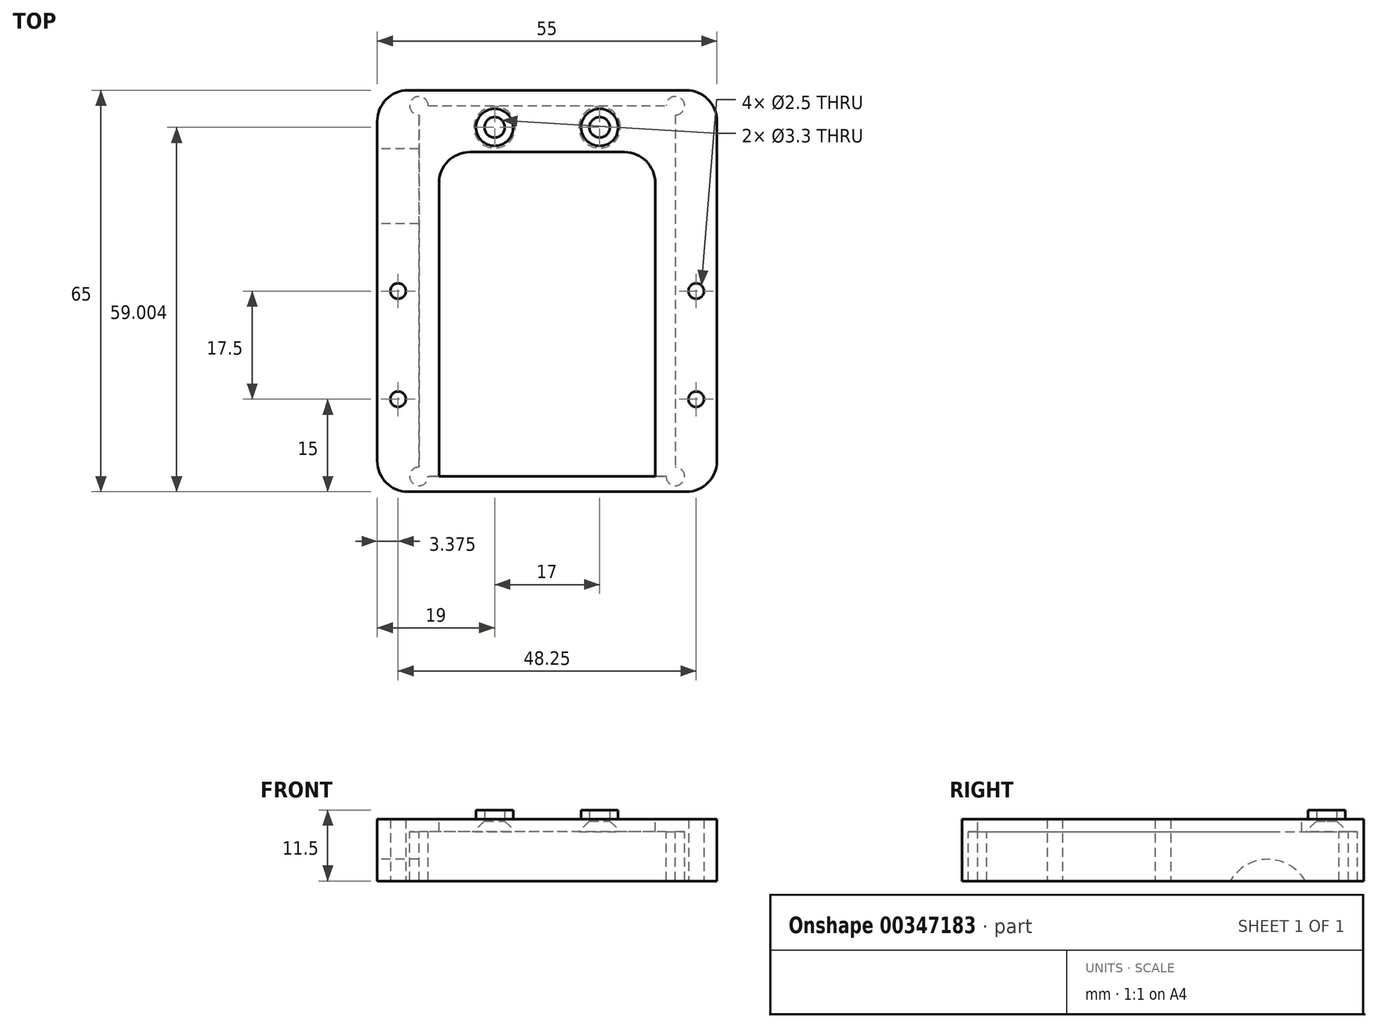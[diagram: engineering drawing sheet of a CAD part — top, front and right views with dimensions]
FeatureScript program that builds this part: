
annotation { "Feature Type Name" : "Feature", "Feature Type Description" : "" }
export const myFeature = defineFeature(function(context is Context, id is Id, definition is map)
    precondition{}
    {
        {
            var Q0;
            Q0=qCreatedBy(makeId("Front.planeOp"),FACE);
            var sketch = newSketch(context, id + "F0", { "sketchPlane" : qUnion([Q0])});
            skLineSegment(sketch, "E0.bottom", {"start": v(27.5, -5) * mm, "end": v(-27.5, -5) * mm});
            skLineSegment(sketch, "E0.top", {"start": v(27.5, 5) * mm, "end": v(-27.5, 5) * mm});
            skLineSegment(sketch, "E0.left", {"start": v(27.5, -5) * mm, "end": v(27.5, 5) * mm});
            skLineSegment(sketch, "E0.right", {"start": v(-27.5, -5) * mm, "end": v(-27.5, 5) * mm});
            skPoint(sketch, "E0.middle", {"position": v(0, 0) * mm});
            skSolve(sketch);
        }
        {
            var Q0;
            Q0 = qSketchRegion(id + "F0", true);
            extrude(context, id + "F1", {"entities" : qUnion([Q0]), "endBound" : BoundingType.SYMMETRIC, "depth" : 65 * mm});
        }
        {
            var Q0;
            Q0=qCreatedBy(makeId("Top.planeOp"),FACE);
            var sketch = newSketch(context, id + "F2", { "sketchPlane" : qUnion([Q0])});
            skPoint(sketch, "E1.middle", {"position": v(0, 0) * mm});
            skPoint(sketch, "E2.visualSharp", {"position": v(17.5, 22.5) * mm});
            skPoint(sketch, "E3.visualSharp", {"position": v(-17.5, 22.5) * mm});
            skLineSegment(sketch, "E4", {"start": v(-17.5, 17.5) * mm, "end": v(-17.5, -30) * mm});
            skLineSegment(sketch, "E5", {"start": v(17.5, 17.5) * mm, "end": v(17.5, -30) * mm});
            skLineSegment(sketch, "E6", {"start": v(17.5, -30) * mm, "end": v(-17.5, -30) * mm});
            skLineSegment(sketch, "E7", {"start": v(-12.5, 22.5) * mm, "end": v(12.5, 22.5) * mm});
            skArc(sketch, "E8.filletArc", {"start": v(17.5, 17.5) * mm, "mid": v(16.04, 21.04) * mm, "end": v(12.5, 22.5) * mm});
            skArc(sketch, "E9.filletArc", {"start": v(-12.5, 22.5) * mm, "mid": v(-16.04, 21.04) * mm, "end": v(-17.5, 17.5) * mm});
            skSolve(sketch);
        }
        {
            var Q0;
            Q0=makeQuery(id+"F1.opExtrude","CAP_EDGE",EDGE,{"disambiguationData":[OSD([sQuery(id+"F0.wireOp",EDGE,"E0.left")])],"isStart":false});
            var Q1;
            Q1=makeQuery(id+"F1.opExtrude","CAP_EDGE",EDGE,{"disambiguationData":[OSD([sQuery(id+"F0.wireOp",EDGE,"E0.right")])],"isStart":false});
            var Q2;
            Q2=makeQuery(id+"F1.opExtrude","CAP_EDGE",EDGE,{"disambiguationData":[OSD([sQuery(id+"F0.wireOp",EDGE,"E0.right")])],"isStart":true});
            var Q3;
            Q3=makeQuery(id+"F1.opExtrude","CAP_EDGE",EDGE,{"disambiguationData":[OSD([sQuery(id+"F0.wireOp",EDGE,"E0.left")])],"isStart":true});
            fillet(context, id + "F3", {"entities" : qUnion([Q0, Q1, Q2, Q3]), "radius" : 5 * mm, "tangentPropagation" : true, "allowEdgeOverflow" : false});
        }
        {
            var Q0;
            Q0 = qSketchRegion(id + "F2", true);
            var Q1;
            Q1=makeQuery(id+"F1.opExtrude","SWEPT_FACE",FACE,{"disambiguationData":[OSD([sQuery(id+"F0.wireOp",EDGE,"E0.top")])]});
            extrude(context, id + "F4", {"entities" : qUnion([Q0]), "operationType" : NewBodyOperationType.REMOVE, "endBound" : BoundingType.SYMMETRIC, "oppositeDirection" : true, "endBoundEntityFace" : qUnion([Q1]), "depth" : 25 * mm});
        }
        {
            var Q0;
            Q0=qCreatedBy(makeId("Top.planeOp"),FACE);
            var sketch = newSketch(context, id + "F5", { "sketchPlane" : qUnion([Q0])});
            skLineSegment(sketch, "E10.bottom", {"start": v(20.75, -30) * mm, "end": v(-20.75, -30) * mm});
            skLineSegment(sketch, "E10.top", {"start": v(20.75, 30) * mm, "end": v(-20.75, 30) * mm});
            skLineSegment(sketch, "E10.left", {"start": v(20.75, -30) * mm, "end": v(20.75, 30) * mm});
            skLineSegment(sketch, "E10.right", {"start": v(-20.75, -30) * mm, "end": v(-20.75, 30) * mm});
            skPoint(sketch, "E10.middle", {"position": v(0, 0) * mm});
            skCircle(sketch, "E11", {"center": v(-20.75, 30) * mm, "radius": 1.5 * mm});
            skCircle(sketch, "E12", {"center": v(20.75, 30) * mm, "radius": 1.5 * mm});
            skCircle(sketch, "E13", {"center": v(-20.75, -30) * mm, "radius": 1.5 * mm});
            skCircle(sketch, "E14", {"center": v(20.75, -30) * mm, "radius": 1.5 * mm});
            skSolve(sketch);
        }
        {
            var Q0;
            Q0 = qSketchRegion(id + "F5", true);
            extrude(context, id + "F6", {"entities" : qUnion([Q0]), "operationType" : NewBodyOperationType.REMOVE, "oppositeDirection" : true, "depth" : 30 * mm});
        }
        {
            var Q0;
            Q0 = qSketchRegion(id + "F5", true);
            extrude(context, id + "F7", {"entities" : qUnion([Q0]), "operationType" : NewBodyOperationType.REMOVE, "depth" : 3 * mm});
        }
        {
            var Q0;
            Q0=makeQuery(id+"F7.boolean.opBoolean","COPY",FACE,{"derivedFrom":makeQuery(id+"F7.opExtrude","CAP_FACE",FACE,{"disambiguationData":[OSD([sQuery(id+"F5.wireOp",EDGE,"E10.bottom"),sQuery(id+"F5.wireOp",EDGE,"E10.top"),sQuery(id+"F5.wireOp",EDGE,"E10.left"),sQuery(id+"F5.wireOp",EDGE,"E10.right"),sQuery(id+"F5.wireOp",EDGE,"E11"),sQuery(id+"F5.wireOp",EDGE,"E12"),sQuery(id+"F5.wireOp",EDGE,"E13"),sQuery(id+"F5.wireOp",EDGE,"E14")])],"isStart":false})});
            var sketch = newSketch(context, id + "F8", { "sketchPlane" : qUnion([Q0])});
            skPoint(sketch, "E15", {"position": v(-8.5, -26.5) * mm});
            skPoint(sketch, "E16", {"position": v(8.5, -26.5) * mm});
            skSolve(sketch);
        }
        {
            var Q0;
            Q0=sQuery(id+"F8.wireOp",VERTEX,"E15");
            var Q1;
            Q1=sQuery(id+"F8.wireOp",VERTEX,"E16");
            var Q2;
            Q2=makeQuery(id+"F1.opExtrude","SWEPT_BODY",BODY,{"disambiguationData":[OSD([sQuery(id+"F0.wireOp",EDGE,"E0.bottom"),sQuery(id+"F0.wireOp",EDGE,"E0.top"),sQuery(id+"F0.wireOp",EDGE,"E0.left"),sQuery(id+"F0.wireOp",EDGE,"E0.right")])]});
            hole(context, id + "F9", {"style" : HoleStyle.C_SINK, "endStyle" : HoleEndStyle.THROUGH, "standardTappedOrClearance" : lookupTablePath({ "standard" : "ISO", "fit" : "Normal", "size" : "M3", "type" : "Clearance" }), "standardBlindInLast" : lookupTablePath({ "fit" : "Standard", "standard" : "ISO", "size" : "M3", "type" : "Clearance" }), "holeDiameter" : 3.3 * mm, "cSinkDiameter" : 6.72 * mm, "cSinkAngle" : 90 * degree, "tappedDepth" : 12 * mm, "tapClearance" : 3, "locations" : qUnion([Q0, Q1]), "scope" : qUnion([Q2])});
        }
        {
            var Q0;
            Q0=makeQuery(id+"F1.opExtrude","SWEPT_FACE",FACE,{"disambiguationData":[OSD([sQuery(id+"F0.wireOp",EDGE,"E0.top")])]});
            var sketch = newSketch(context, id + "F10", { "sketchPlane" : qUnion([Q0])});
            skCircle(sketch, "E17", {"center": v(8.5, 26.5) * mm, "radius": 3 * mm});
            skCircle(sketch, "E18", {"center": v(-8.5, 26.5) * mm, "radius": 3 * mm});
            skSolve(sketch);
        }
        {
            var Q0;
            Q0 = qSketchRegion(id + "F10", true);
            extrude(context, id + "F11", {"entities" : qUnion([Q0]), "operationType" : NewBodyOperationType.ADD, "depth" : 1.5 * mm});
        }
        {
            var Q0;
            Q0=sQuery(id+"F8.wireOp",VERTEX,"E15");
            var Q1;
            Q1=sQuery(id+"F8.wireOp",VERTEX,"E16");
            var Q2;
            Q2=sQuery(id+"F8.wireOp",VERTEX,"94b8a258-85e8-4356-9477-375777d7274d");
            var Q3;
            Q3=sQuery(id+"F8.wireOp",VERTEX,"40654904-7518-4712-aa85-c7850a164911");
            var Q4;
            Q4=makeQuery(id+"F1.opExtrude","SWEPT_BODY",BODY,{"disambiguationData":[OSD([sQuery(id+"F0.wireOp",EDGE,"E0.bottom"),sQuery(id+"F0.wireOp",EDGE,"E0.top"),sQuery(id+"F0.wireOp",EDGE,"E0.left"),sQuery(id+"F0.wireOp",EDGE,"E0.right")])]});
            hole(context, id + "F12", {"style" : HoleStyle.C_SINK, "endStyle" : HoleEndStyle.BLIND, "standardTappedOrClearance" : lookupTablePath({ "standard" : "ISO", "fit" : "Normal", "size" : "M3", "type" : "Clearance" }), "standardBlindInLast" : lookupTablePath({ "fit" : "Standard", "standard" : "ISO", "size" : "M3", "type" : "Clearance" }), "holeDiameter" : 3.3 * mm, "cSinkDiameter" : 6.72 * mm, "cSinkAngle" : 90 * degree, "holeDepth" : 13.5 * mm, "tappedDepth" : 12 * mm, "tapClearance" : 3, "locations" : qUnion([Q0, Q1, Q2, Q3]), "scope" : qUnion([Q4])});
        }
        {
            var Q0;
            Q0=makeQuery(id+"F1.opExtrude","SWEPT_FACE",FACE,{"disambiguationData":[OSD([sQuery(id+"F0.wireOp",EDGE,"E0.bottom")])]});
            var sketch = newSketch(context, id + "F13", { "sketchPlane" : qUnion([Q0])});
            skPoint(sketch, "E19", {"position": v(-24.12, 0) * mm});
            skPoint(sketch, "E20", {"position": v(24.12, 0) * mm});
            skPoint(sketch, "E21", {"position": v(-24.12, 17.5) * mm});
            skPoint(sketch, "E22", {"position": v(24.12, 17.5) * mm});
            skSolve(sketch);
        }
        {
            var Q0;
            Q0=sQuery(id+"F13.wireOp",VERTEX,"E19");
            var Q1;
            Q1=sQuery(id+"F13.wireOp",VERTEX,"E20");
            var Q2;
            Q2=sQuery(id+"F13.wireOp",VERTEX,"E21");
            var Q3;
            Q3=sQuery(id+"F13.wireOp",VERTEX,"E22");
            var Q4;
            Q4=makeQuery(id+"F1.opExtrude","SWEPT_BODY",BODY,{"disambiguationData":[OSD([sQuery(id+"F0.wireOp",EDGE,"E0.bottom"),sQuery(id+"F0.wireOp",EDGE,"E0.top"),sQuery(id+"F0.wireOp",EDGE,"E0.left"),sQuery(id+"F0.wireOp",EDGE,"E0.right")])]});
            hole(context, id + "F14", {"style" : HoleStyle.SIMPLE, "endStyle" : HoleEndStyle.BLIND, "standardTappedOrClearance" : lookupTablePath({ "standard" : "ISO", "engagement" : "75%", "pitch" : "0.5 mm", "size" : "M3", "type" : "Tapped" }), "standardBlindInLast" : lookupTablePath({ "standard" : "ISO", "engagement" : "75%", "pitch" : "0.5 mm", "size" : "M3", "type" : "Tapped" }), "holeDiameter" : 2.5 * mm, "showTappedDepth" : true, "holeDepth" : 13.5 * mm, "tappedDepth" : 12 * mm, "tapClearance" : 3, "locations" : qUnion([Q0, Q1, Q2, Q3]), "scope" : qUnion([Q4]), "majorDiameter" : 3 * mm});
        }
        {
            var Q0;
            Q0=makeQuery(id+"F1.opExtrude","SWEPT_FACE",FACE,{"disambiguationData":[OSD([sQuery(id+"F0.wireOp",EDGE,"E0.right")])]});
            var sketch = newSketch(context, id + "F15", { "sketchPlane" : qUnion([Q0])});
            skPoint(sketch, "E23", {"position": v(-16.97, -8.5) * mm});
            skCircle(sketch, "E24", {"center": v(-16.97, -8.5) * mm, "radius": 7 * mm});
            skSolve(sketch);
        }
        {
            var Q0;
            {var subQ0=sQuery(id+"F15.wireOp",EDGE,"E24");var subQ1=makeQuery(id+"F1.opExtrude","SWEPT_EDGE",EDGE,{"disambiguationData":[OSD([sQuery(id+"F0.wireOp",EDGE,"E0.bottom"),sQuery(id+"F0.wireOp",EDGE,"E0.right")])]});var subQ2=makeQuery(id+"F15.imprint","INTERSECT",VERTEX,{"disambiguationData":[OD(0.0)],"derivedFrom":[subQ1,subQ0]});Q0=makeQuery(id+"F15.imprint","IMPRINT",FACE,{"disambiguationData":[TD([[makeQuery(id+"F15.imprint","IMPRINT",EDGE,{"disambiguationData":[TD([[subQ2,1.0]])],"derivedFrom":subQ0}),1.0]])]});}
            extrude(context, id + "F16", {"entities" : qUnion([Q0]), "operationType" : NewBodyOperationType.REMOVE, "oppositeDirection" : true, "depth" : 12 * mm});
        }
    });
